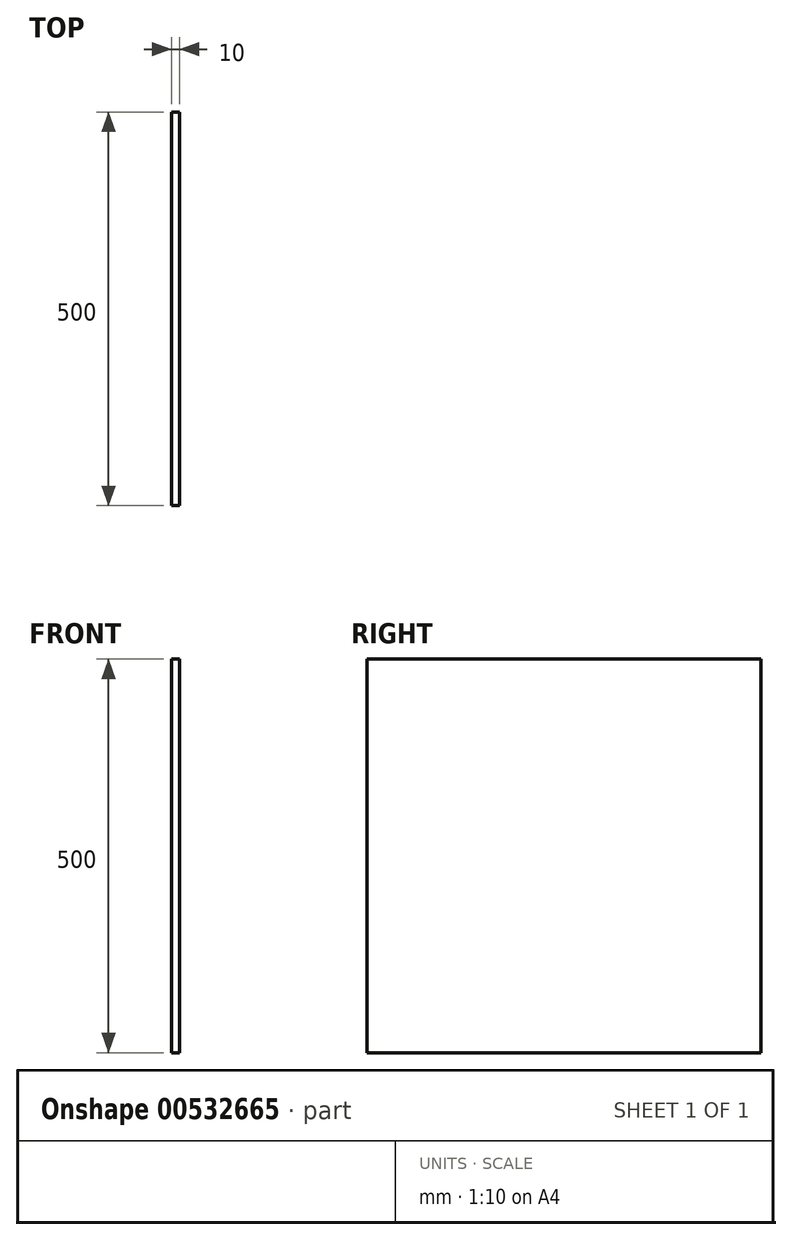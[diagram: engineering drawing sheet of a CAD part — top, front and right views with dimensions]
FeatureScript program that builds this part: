
annotation { "Feature Type Name" : "Feature", "Feature Type Description" : "" }
export const myFeature = defineFeature(function(context is Context, id is Id, definition is map)
    precondition{}
    {
        {
            var Q0;
            Q0=qCreatedBy(makeId("Front.planeOp"),FACE);
            var sketch = newSketch(context, id + "F0", { "sketchPlane" : qUnion([Q0])});
            skLineSegment(sketch, "E0.bottom", {"start": v(-5, 250) * mm, "end": v(5, 250) * mm});
            skLineSegment(sketch, "E0.top", {"start": v(-5, -250) * mm, "end": v(5, -250) * mm});
            skLineSegment(sketch, "E0.left", {"start": v(-5, 250) * mm, "end": v(-5, -250) * mm});
            skLineSegment(sketch, "E0.right", {"start": v(5, 250) * mm, "end": v(5, -250) * mm});
            skPoint(sketch, "E0.middle", {"position": v(0, 0) * mm});
            skSolve(sketch);
        }
        {
            var Q0;
            Q0 = qSketchRegion(id + "F0", true);
            extrude(context, id + "F1", {"entities" : qUnion([Q0]), "endBound" : BoundingType.SYMMETRIC, "depth" : 500 * mm, "offsetDistance" : 25 * mm});
        }
    });
